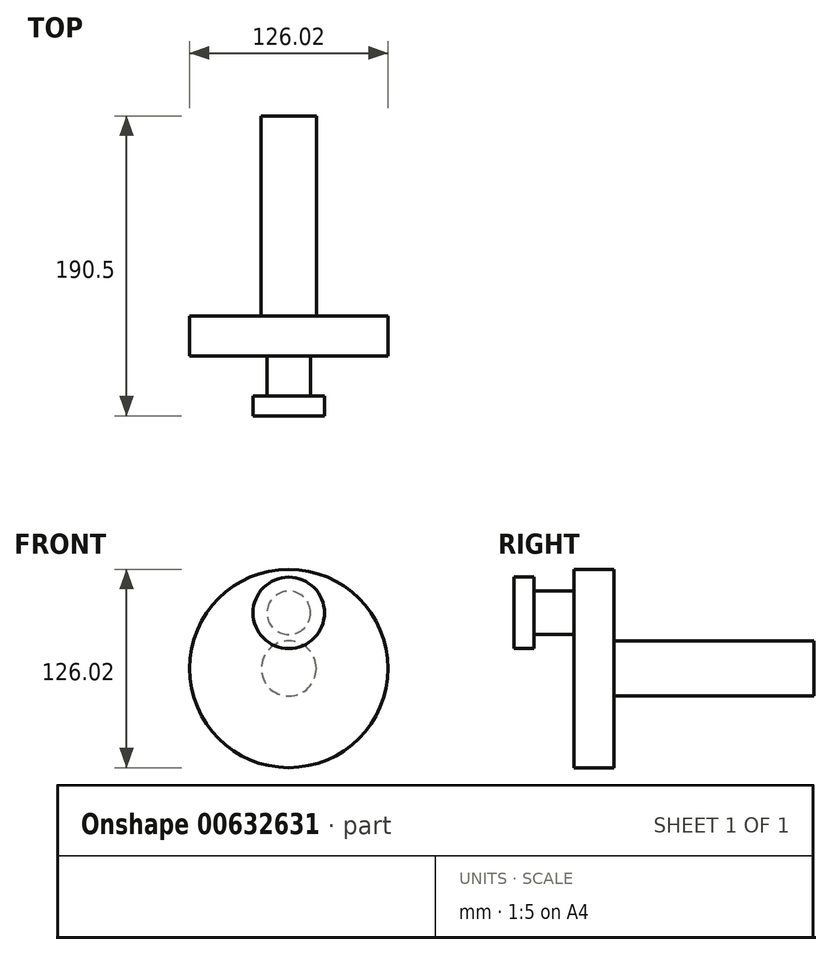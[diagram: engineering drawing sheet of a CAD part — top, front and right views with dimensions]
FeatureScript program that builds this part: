
annotation { "Feature Type Name" : "Feature", "Feature Type Description" : "" }
export const myFeature = defineFeature(function(context is Context, id is Id, definition is map)
    precondition{}
    {
        {
            var Q0;
            Q0=qCreatedBy(makeId("Front.planeOp"),FACE);
            var sketch = newSketch(context, id + "F0", { "sketchPlane" : qUnion([Q0])});
            skCircle(sketch, "E0", {"center": v(0, 0) * mm, "radius": 63 * mm});
            skSolve(sketch);
        }
        {
            var Q0;
            Q0 = qSketchRegion(id + "F0", true);
            extrude(context, id + "F1", {"entities" : qUnion([Q0]), "depth" : 25.4 * mm, "offsetDistance" : 25.4 * mm});
        }
        {
            var Q0;
            Q0=qCreatedBy(makeId("Front.planeOp"),FACE);
            var sketch = newSketch(context, id + "F2", { "sketchPlane" : qUnion([Q0])});
            skCircle(sketch, "E1", {"center": v(0, 35.3) * mm, "radius": 13.8 * mm});
            skSolve(sketch);
        }
        {
            var Q0;
            Q0 = qSketchRegion(id + "F2", true);
            extrude(context, id + "F3", {"entities" : qUnion([Q0]), "operationType" : NewBodyOperationType.ADD, "depth" : 63.5 * mm, "offsetDistance" : 25.4 * mm});
        }
        {
            var Q0;
            Q0=makeQuery(id+"F3.opExtrude","CAP_FACE",FACE,{"disambiguationData":[OSD([sQuery(id+"F2.wireOp",EDGE,"E1")])],"isStart":false});
            var sketch = newSketch(context, id + "F4", { "sketchPlane" : qUnion([Q0])});
            skCircle(sketch, "E2", {"center": v(0, 35.3) * mm, "radius": 22.7 * mm});
            skSolve(sketch);
        }
        {
            var Q0;
            Q0 = qSketchRegion(id + "F4", true);
            extrude(context, id + "F5", {"entities" : qUnion([Q0]), "operationType" : NewBodyOperationType.ADD, "depth" : -12.7 * mm, "offsetDistance" : 25.4 * mm});
        }
        {
            var Q0;
            Q0=makeQuery(id+"F1.opExtrude","CAP_FACE",FACE,{"disambiguationData":[OSD([sQuery(id+"F0.wireOp",EDGE,"E0")])],"isStart":true});
            var sketch = newSketch(context, id + "F6", { "sketchPlane" : qUnion([Q0])});
            skCircle(sketch, "E3", {"center": v(0, 0) * mm, "radius": 17.49 * mm});
            skSolve(sketch);
        }
        {
            var Q0;
            Q0 = qSketchRegion(id + "F6", true);
            extrude(context, id + "F7", {"entities" : qUnion([Q0]), "operationType" : NewBodyOperationType.ADD, "depth" : 127 * mm, "offsetDistance" : 25.4 * mm});
        }
    });
